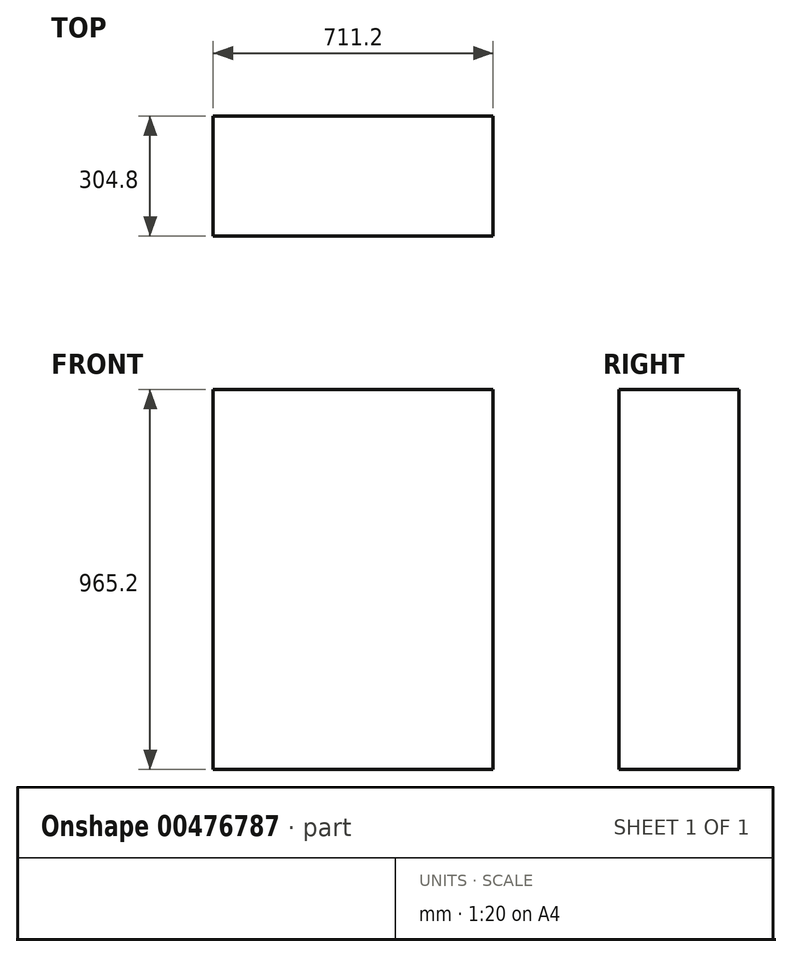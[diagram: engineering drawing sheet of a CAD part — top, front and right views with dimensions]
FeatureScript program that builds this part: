
annotation { "Feature Type Name" : "Feature", "Feature Type Description" : "" }
export const myFeature = defineFeature(function(context is Context, id is Id, definition is map)
    precondition{}
    {
        {
            var Q0;
            Q0=qCreatedBy(makeId("Top.planeOp"),FACE);
            var sketch = newSketch(context, id + "F0", { "sketchPlane" : qUnion([Q0])});
            skLineSegment(sketch, "E0.bottom", {"start": v(0, 0) * mm, "end": v(711.2, 0) * mm});
            skLineSegment(sketch, "E0.top", {"start": v(0, 304.8) * mm, "end": v(711.2, 304.8) * mm});
            skLineSegment(sketch, "E0.left", {"start": v(0, 0) * mm, "end": v(0, 304.8) * mm});
            skLineSegment(sketch, "E0.right", {"start": v(711.2, 0) * mm, "end": v(711.2, 304.8) * mm});
            skSolve(sketch);
        }
        {
            var Q0;
            Q0=qSketchRegion(id+"F0",true);
            extrude(context, id + "F1", {"entities" : qUnion([Q0]), "depth" : 965.2 * mm});
        }
    });
